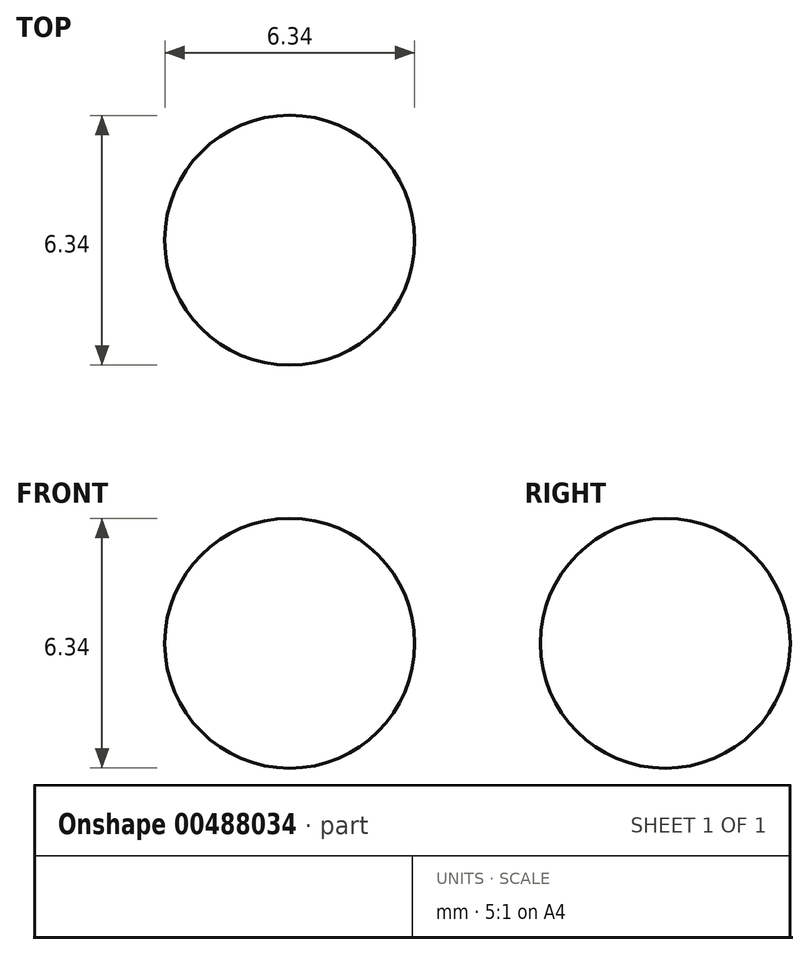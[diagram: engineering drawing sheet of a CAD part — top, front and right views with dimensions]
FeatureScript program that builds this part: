
annotation { "Feature Type Name" : "Feature", "Feature Type Description" : "" }
export const myFeature = defineFeature(function(context is Context, id is Id, definition is map)
    precondition{}
    {
        {
            var Q0;
            Q0=qCreatedBy(makeId("Front.planeOp"),FACE);
            var sketch = newSketch(context, id + "F0", { "sketchPlane" : qUnion([Q0])});
            skLineSegment(sketch, "E0", {"start": v(0, 3.18) * mm, "end": v(0, -3.18) * mm});
            skArc(sketch, "E1", {"start": v(0, -3.18) * mm, "mid": v(3.18, 0) * mm, "end": v(0, 3.18) * mm});
            skSolve(sketch);
        }
        {
            var Q0;
            Q0=makeQuery(id+"F0.imprint","IMPRINT",FACE,{"disambiguationData":[TD([[makeQuery(id+"F0.imprint","IMPRINT",EDGE,{"derivedFrom":sQuery(id+"F0.wireOp",EDGE,"E0")}),1.0]])]});
            var Q1;
            Q1=sQuery(id+"F0.wireOp",EDGE,"E0");
            revolve(context, id + "F1", {"entities" : qUnion([Q0]), "axis" : qUnion([Q1]), "revolveType" : RevolveType.FULL});
        }
    });
